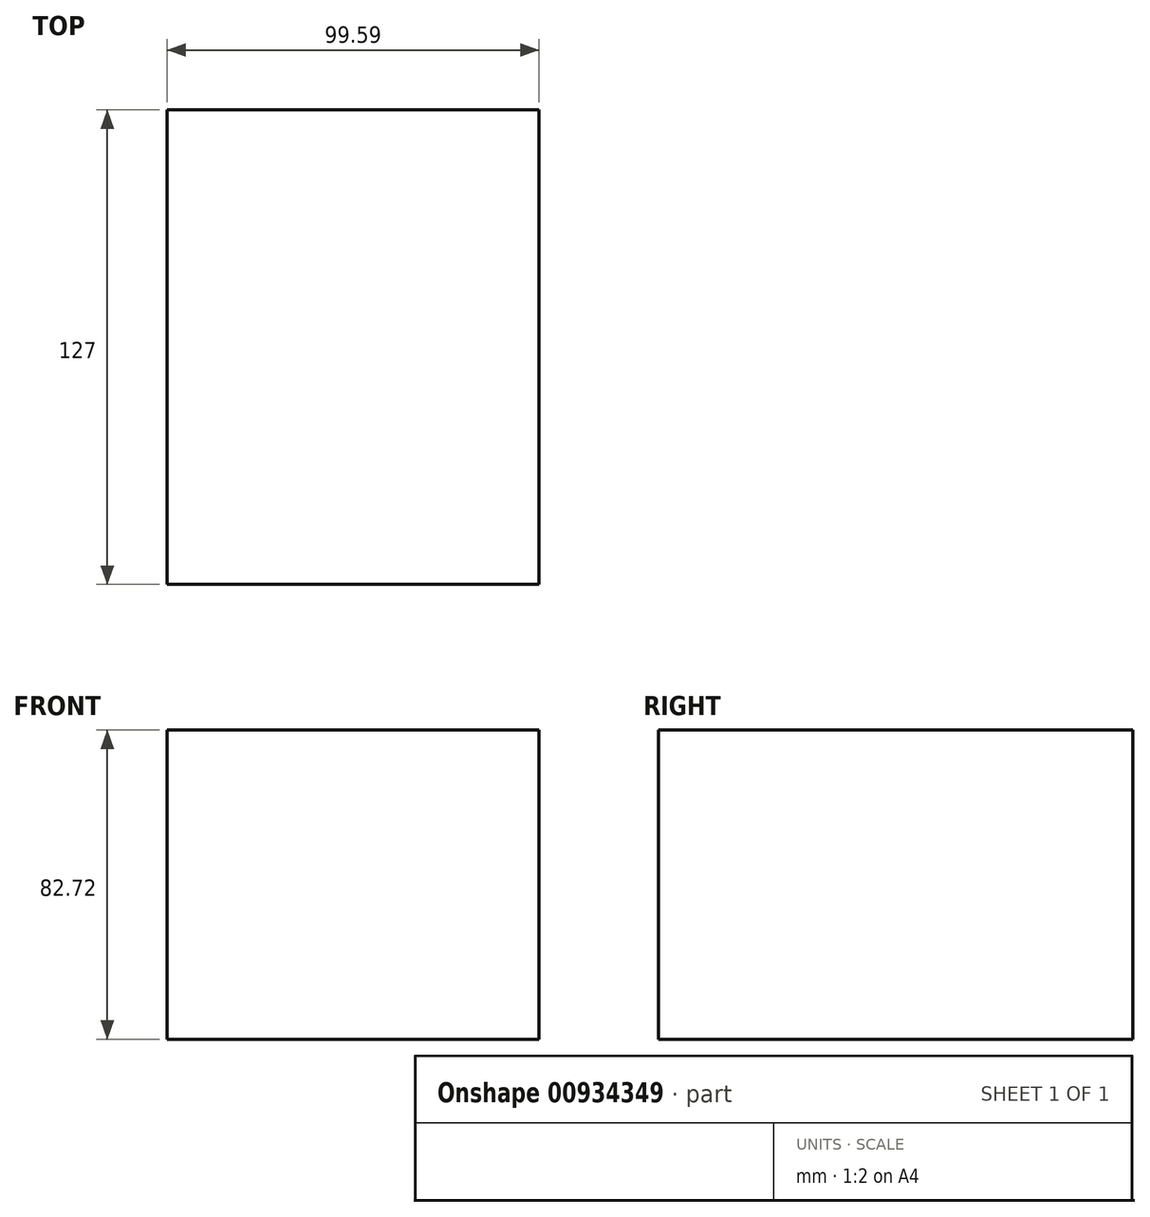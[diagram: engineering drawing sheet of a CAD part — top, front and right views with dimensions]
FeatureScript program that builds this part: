
annotation { "Feature Type Name" : "Feature", "Feature Type Description" : "" }
export const myFeature = defineFeature(function(context is Context, id is Id, definition is map)
    precondition{}
    {
        {
            var Q0;
            Q0=qCreatedBy(makeId("Front.planeOp"),FACE);
            var sketch = newSketch(context, id + "F0", { "sketchPlane" : qUnion([Q0])});
            skLineSegment(sketch, "E0", {"start": v(-48.58, 42.56) * mm, "end": v(-48.58, -40.16) * mm});
            skLineSegment(sketch, "E1", {"start": v(-48.58, -40.16) * mm, "end": v(51.01, -40.16) * mm});
            skLineSegment(sketch, "E2", {"start": v(51.01, -40.16) * mm, "end": v(51.01, 42.56) * mm});
            skLineSegment(sketch, "E3", {"start": v(51.01, 42.56) * mm, "end": v(-48.58, 42.56) * mm});
            skSolve(sketch);
        }
        {
            var Q0;
            Q0 = qSketchRegion(id + "F0", true);
            extrude(context, id + "F1", {"entities" : qUnion([Q0]), "depth" : 127 * mm, "offsetDistance" : 25.4 * mm});
        }
    });
